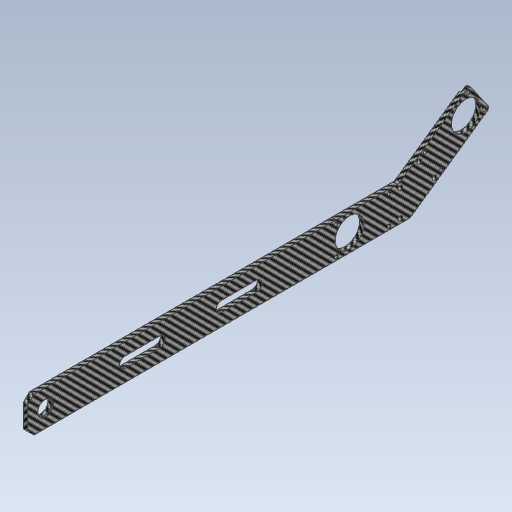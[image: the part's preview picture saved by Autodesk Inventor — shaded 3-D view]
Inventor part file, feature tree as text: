
AUTODESK INVENTOR PART (.ipt)
format: ipt  version: 2024 (Build 280153000, 153)  size: 245,760 bytes
history: native  units: mm
features: other x4, chamfer x3, extrude x1, sketch x1
ambient origin geometry x8: Origin, YZ Plane, XZ Plane, XY Plane, X Axis, Y Axis, Z Axis, Center Point
bodies: Body1 (feature_tree)
feature tree (9):
  other  "_bridseye_sketch.ipt"
  chamfer  "面取り1"  Distance=10.0mm
  chamfer  "面取り2"  Distance=1.0mm Angle=45.0deg
  extrude  "押し出し1"  Depth=1.0mm TaperAngle=0.0deg
  chamfer  "面取り3"  Distance=2.0mm Angle=45.0deg
  other  "ソリッド6::_bridseye_sketch.ipt"
  other  "TaggingFeature1"
  other  "side_links-link1_link1Conn"
  sketch  "スケッチ2"
